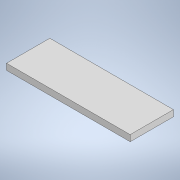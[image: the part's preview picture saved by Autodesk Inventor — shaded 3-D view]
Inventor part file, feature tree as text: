
AUTODESK INVENTOR PART (.ipt)
format: ipt  version: 2021 (Build 250183000, 183)  size: 90,624 bytes
history: native  units: mm
features: extrude x1, sketch x1
ambient origin geometry x8: Origin, YZ Plane, XZ Plane, XY Plane, X Axis, Y Axis, Z Axis, Center Point
bodies: Solid1 (feature_tree)
feature tree (2):
  extrude  "Extrusion1"  Depth=40.0mm
  sketch  "Sketch1"  dims[d0=14.0mm d1=40.0mm d2=2.0mm d3=0.0mm]
